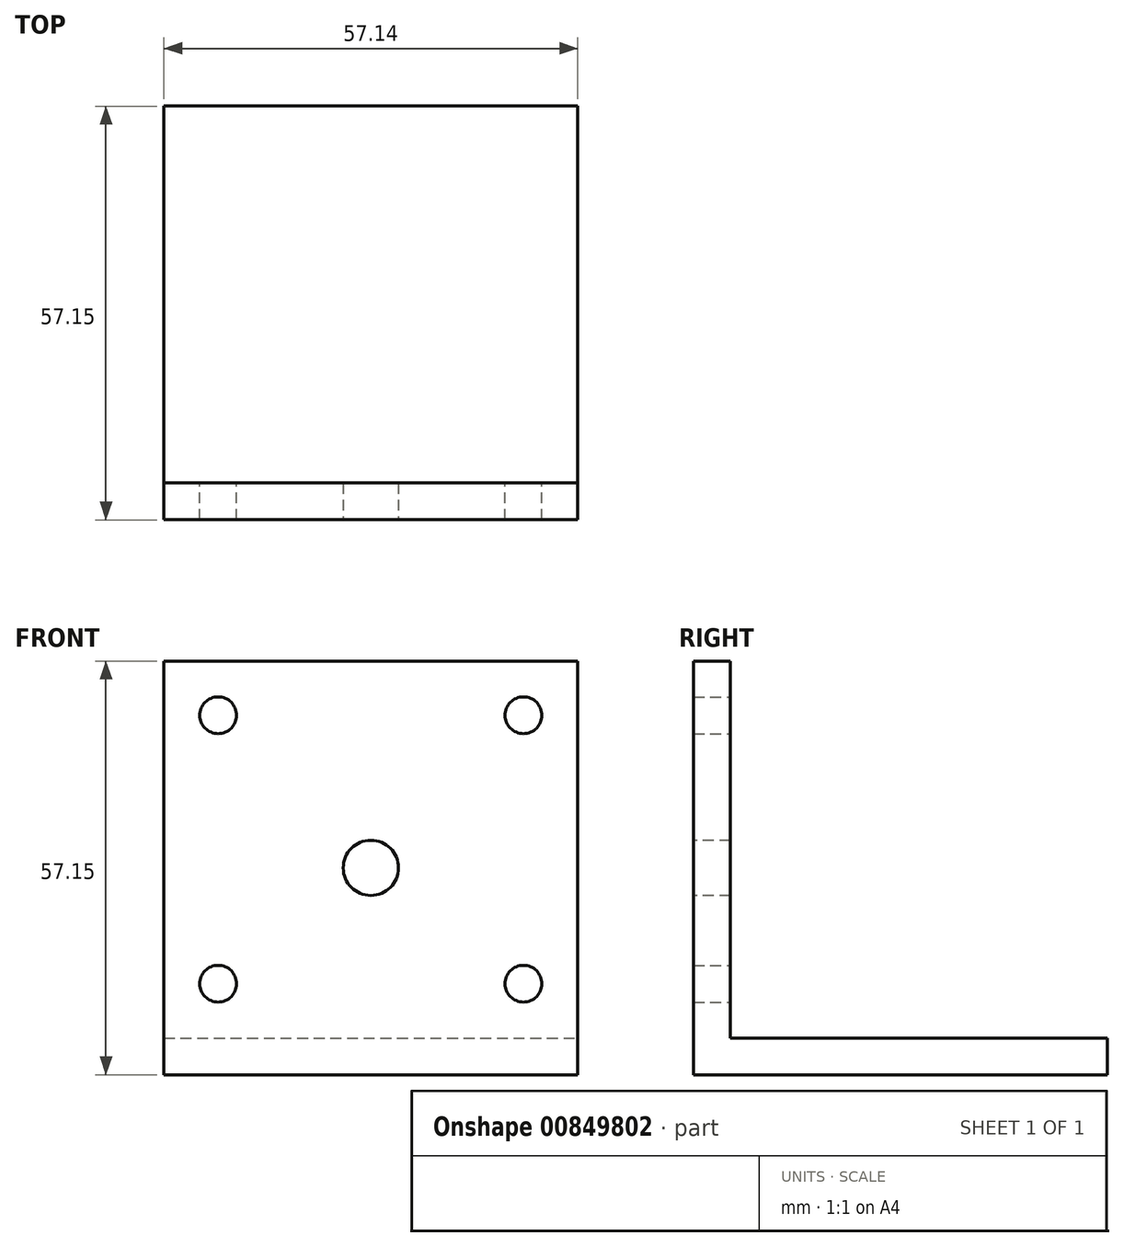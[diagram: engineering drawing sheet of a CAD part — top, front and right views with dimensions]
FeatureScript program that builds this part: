
annotation { "Feature Type Name" : "Feature", "Feature Type Description" : "" }
export const myFeature = defineFeature(function(context is Context, id is Id, definition is map)
    precondition{}
    {
        {
            var Q0;
            Q0=qCreatedBy(makeId("Top.planeOp"),FACE);
            var sketch = newSketch(context, id + "F0", { "sketchPlane" : qUnion([Q0])});
            skLineSegment(sketch, "E0.bottom", {"start": v(-28.57, 28.57) * mm, "end": v(28.58, 28.57) * mm});
            skLineSegment(sketch, "E0.top", {"start": v(-28.58, -28.57) * mm, "end": v(28.57, -28.57) * mm});
            skLineSegment(sketch, "E0.left", {"start": v(-28.57, 28.58) * mm, "end": v(-28.58, -28.57) * mm});
            skLineSegment(sketch, "E0.right", {"start": v(28.58, 28.57) * mm, "end": v(28.57, -28.58) * mm});
            skPoint(sketch, "E0.middle", {"position": v(0, 0) * mm});
            skSolve(sketch);
        }
        {
            var Q0;
            Q0=makeQuery(id+"F0.imprint","IMPRINT",FACE,{"disambiguationData":[TD([[makeQuery(id+"F0.imprint","IMPRINT",EDGE,{"derivedFrom":sQuery(id+"F0.wireOp",EDGE,"E0.bottom")}),-1.0]])]});
            extrude(context, id + "F1", {"entities" : qUnion([Q0]), "depth" : 57.15 * mm, "offsetDistance" : 25.4 * mm});
        }
        {
            var Q0;
            Q0=makeQuery(id+"F1.opExtrude","CAP_FACE",FACE,{"disambiguationData":[OSD([sQuery(id+"F0.wireOp",EDGE,"E0.bottom"),sQuery(id+"F0.wireOp",EDGE,"E0.top"),sQuery(id+"F0.wireOp",EDGE,"E0.left"),sQuery(id+"F0.wireOp",EDGE,"E0.right")])],"isStart":false});
            var Q1;
            Q1=makeQuery(id+"F1.opExtrude","SWEPT_FACE",FACE,{"disambiguationData":[OSD([sQuery(id+"F0.wireOp",EDGE,"E0.right")])]});
            var Q2;
            Q2=makeQuery(id+"F1.opExtrude","SWEPT_FACE",FACE,{"disambiguationData":[OSD([sQuery(id+"F0.wireOp",EDGE,"E0.bottom")])]});
            var Q3;
            Q3=makeQuery(id+"F1.opExtrude","SWEPT_FACE",FACE,{"disambiguationData":[OSD([sQuery(id+"F0.wireOp",EDGE,"E0.left")])]});
            shell(context, id + "F2", {"entities" : qUnion([Q0, Q1, Q2, Q3]), "thickness" : 5.08 * mm});
        }
        {
            var Q0;
            Q0=makeQuery(id+"F2.opShell","OFFSET_FACE",FACE,{"disambiguationData":[OSD([sQuery(id+"F0.wireOp",EDGE,"E0.top")])]});
            var sketch = newSketch(context, id + "F3", { "sketchPlane" : qUnion([Q0])});
            skCircle(sketch, "E1", {"center": v(-21.08, 49.66) * mm, "radius": 2.54 * mm});
            skCircle(sketch, "E2.MirrorC", {"center": v(21.08, 49.66) * mm, "radius": 2.54 * mm});
            skCircle(sketch, "E3.MirrorC", {"center": v(-21.08, 12.57) * mm, "radius": 2.54 * mm});
            skCircle(sketch, "E4.MirrorC", {"center": v(21.08, 12.57) * mm, "radius": 2.54 * mm});
            skSolve(sketch);
        }
        {
            var Q0;
            Q0 = qSketchRegion(id + "F3", true);
            extrude(context, id + "F4", {"entities" : qUnion([Q0]), "operationType" : NewBodyOperationType.REMOVE, "oppositeDirection" : true, "depth" : 25.4 * mm, "offsetDistance" : 25.4 * mm});
        }
        {
            var Q0;
            Q0=makeQuery(id+"F1.opExtrude","SWEPT_FACE",FACE,{"disambiguationData":[OSD([sQuery(id+"F0.wireOp",EDGE,"E0.top")])]});
            var sketch = newSketch(context, id + "F5", { "sketchPlane" : qUnion([Q0])});
            skCircle(sketch, "E5", {"center": v(0, 28.58) * mm, "radius": 3.81 * mm});
            skSolve(sketch);
        }
        {
            var Q0;
            Q0=makeQuery(id+"F5.imprint","IMPRINT",FACE,{"disambiguationData":[TD([[makeQuery(id+"F5.imprint","IMPRINT",EDGE,{"derivedFrom":sQuery(id+"F5.wireOp",EDGE,"E5")}),1.0]])]});
            var Q1;
            Q1=sQuery(id+"F5.wireOp",EDGE,"E5");
            extrude(context, id + "F6", {"entities" : qUnion([Q0]), "operationType" : NewBodyOperationType.REMOVE, "surfaceEntities" : qUnion([Q1]), "oppositeDirection" : true, "depth" : 25.4 * mm, "offsetDistance" : 25.4 * mm});
        }
    });
